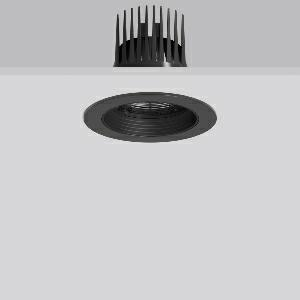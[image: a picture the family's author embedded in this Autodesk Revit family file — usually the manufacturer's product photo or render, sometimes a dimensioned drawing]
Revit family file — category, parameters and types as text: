
# Revit family: heledon_maxi_e_901775_003_76_522e
name_source: partatom
category: Lighting Fixtures
units: mm (PartAtom-declared; Revit-internal decimal feet)

## family parameters
Cut with Voids When Loaded = No
Host = Face
Light Source = No
Part Type = Normal
Room Calculation Point = No
Round Connector Dimension = Use Diameter
Shared = No

## types (1)
- HELEDON maxi E (1 x LED Modul 932 fresh meat, 1750 lm, 3200)
    Apparent Load = 33 VA
    Approval mark = CE
    CIE Flux Codes = 96 99 100 100 100
    Color Rendering = 90
    Color Temperature = 3200
    Default Elevation = 1800 mm
    Description = Series: HELEDON maxi
Round recessed downlight. Housing: die-cast aluminium, powder-coated. Black plastic ring and recessed LED to prevent glare from the side. Optical assembly with lens made of plastic (polycarbonate) for the best homogeneous light distribution - can be changed without tools. Special LED for illumination of meat included. Suitable for Recessed ceiling mounting. Installation without tools thanks to spring fastening system. Including separate LED converter with connecting cable 600 mm.High quality converter without flickering and stroboscopic effect. Through-wiring box (5 pole) available as accessory. The following accessories can be mounted without use of tools: interchangeable lenses, decorative glasses, honeycomb louvre, clear and frosted diffusers, white interchangeable plastic ring. 
Colour: deep black, matt (RAL 9005)
Diameter: 162 mm
Height: 3 mm
Cut-out diameter: 152 mm
Recess height: 200 mm
Luminaire: recess height: 135 mm
Lamp: LED
Socket: without socket
Colour temperature: fresh meat
System power: 33 W
Rated luminous flux: 1750 lm
Luminous efficiency: 53 lm/W
Control gear: Converter, dimmable, DALI
Protection class: II
Type of protection: IP 20
    Height = 0 mm  [stored 0 ft]
    Lamp = 1 x LED Modul 932 fresh meat
    Lamp Light Flux = 1750 lm
    Lamp count = 1
    Length = 162 mm
    Lifetime = 50000 h
    Luminous efficacy = 53 lm/W
    Manufacturer = RZB
    ModVariant = No
    Model = 901775.003.76
    Mounting Place = Ceiling
    Mounting Type = Recessed
    Number of Poles = 1
    OnlyDefault = Yes
    Power Factor = 1
    Product Name = HELEDON maxi E
    Product group = Recessed downlights
    ProductGroupID = 402
    Protection Class = Protection class II
    Protection Degree = IP 20
    RLX_Detail_Level = 1
    RLX_Emergency_Light_Flux = 0 lm
    RLX_Emergency_Type = 0
    RLX_Emergency_Type_DB = No
    RlxData = <blob elided: 122565 chars, md5=16a3eb64>
    Socket = socket
    Standby Power = 0 W
    System Light Flux = 1750 lm
    System Power = 33 W
    Type Comments = Product without accessories
    Type Image = 901663.003.jpg
    URL = http://relux.com
    VarID = ---
    Voltage = 230 V
    Voltage Range = 220-240 V
    Weight = 0.00 kg
    Width = 0 mm  [stored 0 ft]

note: [stored X ft] marks values corroborated as IEEE doubles in the binary element streams (Revit-internal decimal feet)

## geometry (parser evidence)
native form markers: Blend x4, Sweep x12
no freeform markers — native parametric forms only
